# Revit family: Surface Mounted Cistern with 90 degree grabrail
name_source: partatom
category: Сантехнические приборы
revit_build: Autodesk Revit 2016 (Build: 20160314_0715(x64)
units: mm (PartAtom-declared; Revit-internal decimal feet)

## family parameters
Всегда вертикально = Да
На основе рабочей плоскости = Нет
Общий = Нет
При загрузке вырезать с полостями = Нет
Размер круглого соединителя = Использовать диаметр
Тип детали = Нормальный
Точка расчета площади = Нет

## types (1)
- RBA4150-101
    Accessible Compliant = AS1428.1-2009 Compliant
    BAR = Stainless Steel, Satin Finish
    Exclusion zone = Да
    GrabRail_Vertical_Offset = 800 мм
    GrabRail_Vertical_calc = 800 мм
    Modified Issue = 20160802.01
    PaperHolder_Horizontal_Offset = 1050 мм
    PaperHolder_Horizontal_calc = 1050 мм
    PaperHolder_Vertical_Offset = 650 мм
    PaperHolder_Vertical_calc = 650 мм
    Группа модели = RBA4150-101
    Изготовитель = RBA Group
    Описание = Accessible Compliant Backrest

## geometry (parser evidence)
native form markers: Blend x114, Sweep x23
no freeform markers — native parametric forms only
